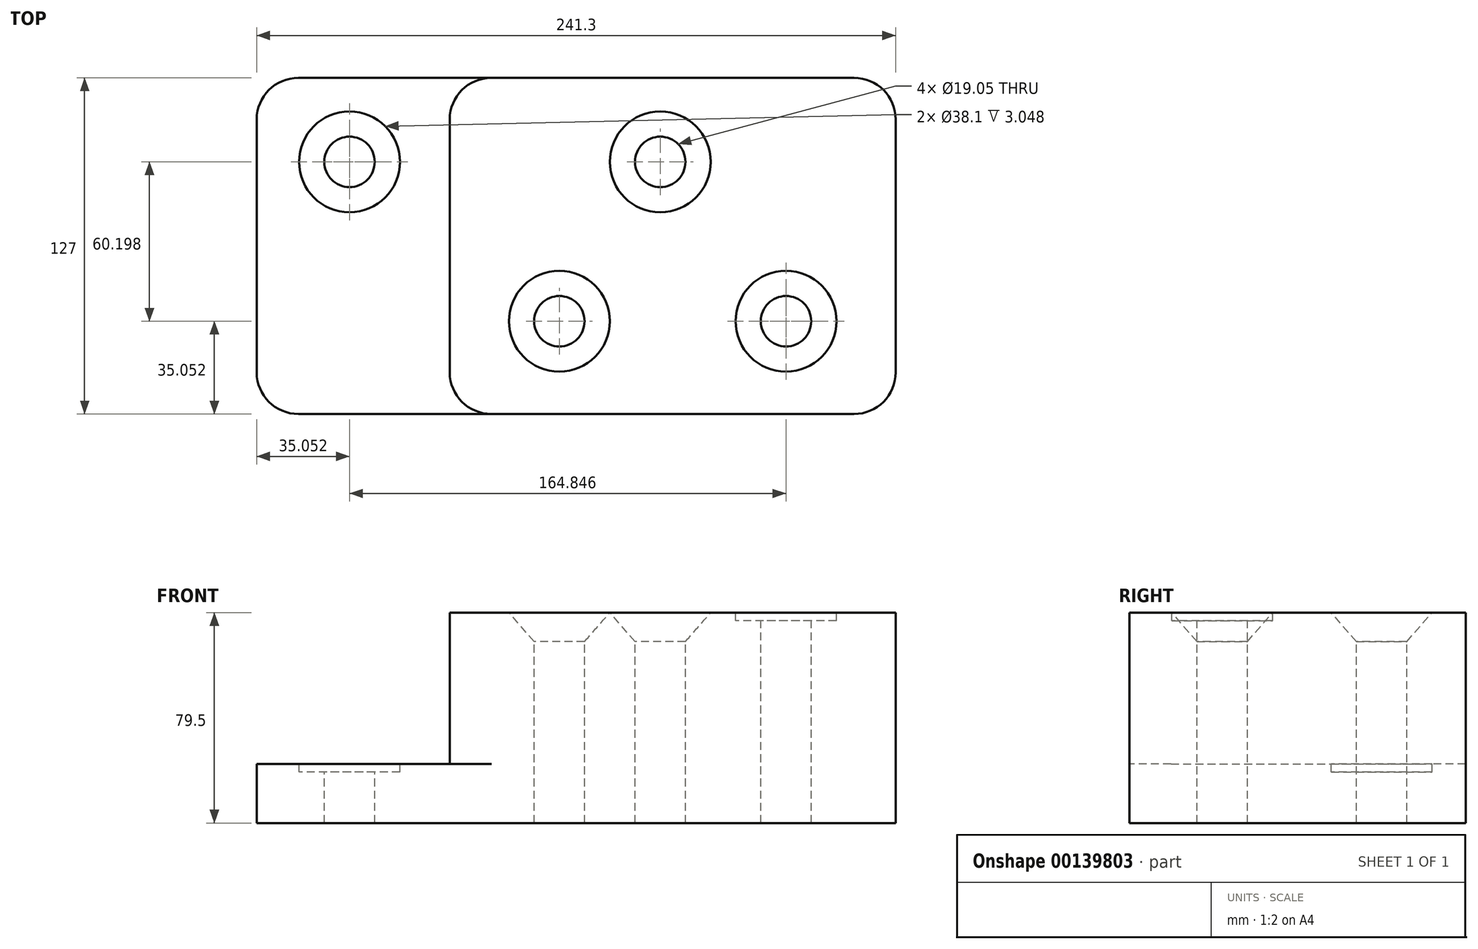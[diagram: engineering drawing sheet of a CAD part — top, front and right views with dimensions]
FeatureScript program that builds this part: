
annotation { "Feature Type Name" : "Feature", "Feature Type Description" : "" }
export const myFeature = defineFeature(function(context is Context, id is Id, definition is map)
    precondition{}
    {
        {
            var Q0;
            Q0=qCreatedBy(makeId("Top.planeOp"),FACE);
            var sketch = newSketch(context, id + "F0", { "sketchPlane" : qUnion([Q0])});
            skLineSegment(sketch, "E0.bottom", {"start": v(0, 0) * mm, "end": v(72.9, 0) * mm});
            skLineSegment(sketch, "E0.top", {"start": v(0, 127) * mm, "end": v(72.9, 127) * mm});
            skLineSegment(sketch, "E0.left", {"start": v(0, 0) * mm, "end": v(0, 127) * mm});
            skLineSegment(sketch, "E0.right", {"start": v(72.9, 0) * mm, "end": v(72.9, 127) * mm});
            skLineSegment(sketch, "E1.bottom", {"start": v(72.9, 127) * mm, "end": v(241.3, 127) * mm});
            skLineSegment(sketch, "E1.top", {"start": v(72.9, 0) * mm, "end": v(241.3, 0) * mm});
            skLineSegment(sketch, "E1.left", {"start": v(72.9, 127) * mm, "end": v(72.9, 0) * mm});
            skLineSegment(sketch, "E1.right", {"start": v(241.3, 127) * mm, "end": v(241.3, 0) * mm});
            skPoint(sketch, "E2", {"position": v(152.4, 95.25) * mm});
            skPoint(sketch, "E3", {"position": v(114.3, 35.05) * mm});
            skPoint(sketch, "E4", {"position": v(35.05, 95.25) * mm});
            skPoint(sketch, "E5", {"position": v(199.9, 35.05) * mm});
            skSolve(sketch);
        }
        {
            var Q0;
            Q0=makeQuery(id+"F0.imprint","IMPRINT",FACE,{"disambiguationData":[TD([[makeQuery(id+"F0.imprint","IMPRINT",EDGE,{"derivedFrom":sQuery(id+"F0.wireOp",EDGE,"E1.bottom")}),-1.0]])]});
            extrude(context, id + "F1", {"entities" : qUnion([Q0]), "depth" : 79.5 * mm});
        }
        {
            var Q0;
            Q0=makeQuery(id+"F0.imprint","IMPRINT",FACE,{"disambiguationData":[TD([[makeQuery(id+"F0.imprint","IMPRINT",EDGE,{"derivedFrom":sQuery(id+"F0.wireOp",EDGE,"E0.bottom")}),1.0]])]});
            extrude(context, id + "F2", {"entities" : qUnion([Q0]), "operationType" : NewBodyOperationType.ADD, "depth" : 22.35 * mm});
        }
        {
            var Q0;
            Q0=makeQuery(id+"F2.opExtrude","SWEPT_EDGE",EDGE,{"disambiguationData":[OSD([sQuery(id+"F0.wireOp",EDGE,"E0.bottom"),sQuery(id+"F0.wireOp",EDGE,"E0.left")])]});
            var Q1;
            Q1=makeQuery(id+"F1.opExtrude","SWEPT_EDGE",EDGE,{"disambiguationData":[OSD([sQuery(id+"F0.wireOp",EDGE,"E0.bottom"),sQuery(id+"F0.wireOp",EDGE,"E1.top"),sQuery(id+"F0.wireOp",EDGE,"E1.left")])]});
            var Q2;
            Q2=makeQuery(id+"F1.opExtrude","SWEPT_EDGE",EDGE,{"disambiguationData":[OSD([sQuery(id+"F0.wireOp",EDGE,"E1.top"),sQuery(id+"F0.wireOp",EDGE,"E1.right")])]});
            var Q3;
            Q3=makeQuery(id+"F1.opExtrude","SWEPT_EDGE",EDGE,{"disambiguationData":[OSD([sQuery(id+"F0.wireOp",EDGE,"E0.top"),sQuery(id+"F0.wireOp",EDGE,"E1.bottom"),sQuery(id+"F0.wireOp",EDGE,"E1.left")])]});
            var Q4;
            Q4=makeQuery(id+"F2.opExtrude","SWEPT_EDGE",EDGE,{"disambiguationData":[OSD([sQuery(id+"F0.wireOp",EDGE,"E0.top"),sQuery(id+"F0.wireOp",EDGE,"E0.left")])]});
            var Q5;
            Q5=makeQuery(id+"F1.opExtrude","SWEPT_EDGE",EDGE,{"disambiguationData":[OSD([sQuery(id+"F0.wireOp",EDGE,"E1.bottom"),sQuery(id+"F0.wireOp",EDGE,"E1.right")])]});
            fillet(context, id + "F3", {"entities" : qUnion([Q0, Q1, Q2, Q3, Q4, Q5]), "radius" : 15.75 * mm, "tangentPropagation" : true, "allowEdgeOverflow" : false});
        }
        {
            var Q0;
            Q0=makeQuery(id+"F1.opExtrude","CAP_FACE",FACE,{"disambiguationData":[OSD([sQuery(id+"F0.wireOp",EDGE,"E1.bottom"),sQuery(id+"F0.wireOp",EDGE,"E1.top"),sQuery(id+"F0.wireOp",EDGE,"E1.left"),sQuery(id+"F0.wireOp",EDGE,"E1.right")])],"isStart":false});
            var sketch = newSketch(context, id + "F4", { "sketchPlane" : qUnion([Q0])});
            skPoint(sketch, "E6", {"position": v(35.05, 95.25) * mm});
            skPoint(sketch, "E7", {"position": v(152.4, 95.25) * mm});
            skPoint(sketch, "E8", {"position": v(199.9, 35.05) * mm});
            skPoint(sketch, "E9", {"position": v(114.3, 35.05) * mm});
            skSolve(sketch);
        }
        {
            var Q0;
            Q0=sQuery(id+"F4.wireOp",VERTEX,"E8");
            var Q1;
            Q1=sQuery(id+"F4.wireOp",VERTEX,"E6");
            var Q2;
            Q2=makeQuery(id+"F1.opExtrude","SWEPT_BODY",BODY,{"disambiguationData":[OSD([sQuery(id+"F0.wireOp",EDGE,"E1.bottom"),sQuery(id+"F0.wireOp",EDGE,"E1.top"),sQuery(id+"F0.wireOp",EDGE,"E1.left"),sQuery(id+"F0.wireOp",EDGE,"E1.right")])]});
            hole(context, id + "F5", {"style" : HoleStyle.C_BORE, "endStyle" : HoleEndStyle.THROUGH, "holeDiameter" : 19.05 * mm, "cBoreDiameter" : 38.1 * mm, "cBoreDepth" : 3.05 * mm, "locations" : qUnion([Q0, Q1]), "scope" : qUnion([Q2]), "isTappedThrough" : true});
        }
        {
            var Q0;
            Q0=sQuery(id+"F4.wireOp",VERTEX,"E7");
            var Q1;
            Q1=sQuery(id+"F4.wireOp",VERTEX,"E9");
            var Q2;
            Q2=makeQuery(id+"F1.opExtrude","SWEPT_BODY",BODY,{"disambiguationData":[OSD([sQuery(id+"F0.wireOp",EDGE,"E1.bottom"),sQuery(id+"F0.wireOp",EDGE,"E1.top"),sQuery(id+"F0.wireOp",EDGE,"E1.left"),sQuery(id+"F0.wireOp",EDGE,"E1.right")])]});
            hole(context, id + "F6", {"style" : HoleStyle.C_SINK, "endStyle" : HoleEndStyle.THROUGH, "holeDiameter" : 19.05 * mm, "cSinkDiameter" : 38.1 * mm, "cSinkAngle" : 82 * degree, "locations" : qUnion([Q0, Q1]), "scope" : qUnion([Q2]), "isTappedThrough" : true});
        }
    });
